# Revit family: Construction_Roof-Accessories_Alpine-SnowGuards_SSG-313H3AL-812BLK
name_source: partatom
category: Specialty Equipment
units: mm (PartAtom-declared; Revit-internal decimal feet)

## family parameters
Cut with Voids When Loaded = No
Host = Face
OmniClass Number = 23.35.20.31.27.14
OmniClass Title = Snow Guards
Part Type = Normal
Room Calculation Point = No
Round Connector Dimension = Use Diameter
Shared = No

## types (1)
- Three Pipe
    Assembly Code = B3010
    Base Material = Alpine SnowGuards - Aluminium - Mill Finish
    Default Elevation = 48"
    Description = SSG-313H3AL-812BLK pipe-style snow guard bracket for composition shingles.
    Edition number = 1
    Horizontal Spacing = 20"
    Keynote = 07720
    Manufacturer = Alpine SnowGuards
    Model = SSG-313H3AL-812BLK
    Pad Material = Alpine SnowGuards - Aluminium - Mill Finish
    Product Guid = af4911d6-feec-4705-85d1-f370e7dd8e1f
    Product Material = Alpine SnowGuards - Aluminium - Mill Finish
    Product data url = https://www.bimobject.com
    URL = https://www.alpinesnowguards.com

## geometry (parser evidence)
native form markers: Sweep x7
no freeform markers — native parametric forms only
